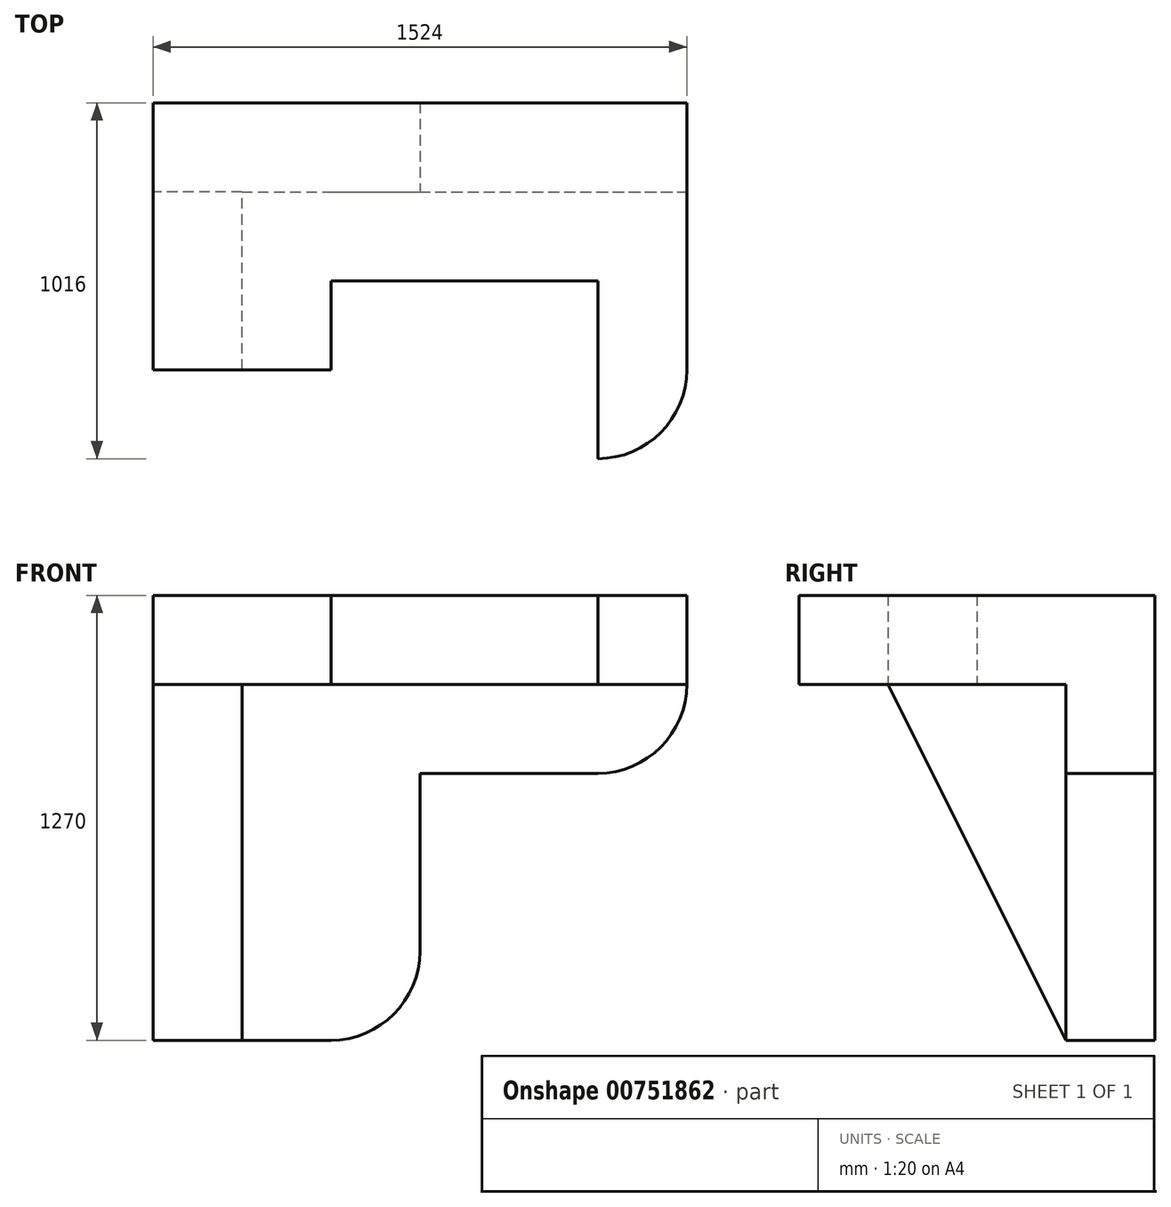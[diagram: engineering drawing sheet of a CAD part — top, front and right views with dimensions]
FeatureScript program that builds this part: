
annotation { "Feature Type Name" : "Feature", "Feature Type Description" : "" }
export const myFeature = defineFeature(function(context is Context, id is Id, definition is map)
    precondition{}
    {
        {
            var Q0;
            Q0=qCreatedBy(makeId("Front.planeOp"),FACE);
            var sketch = newSketch(context, id + "F0", { "sketchPlane" : qUnion([Q0])});
            skLineSegment(sketch, "E0", {"start": v(0, 508) * mm, "end": v(0, -762) * mm});
            skLineSegment(sketch, "E1", {"start": v(0, -762) * mm, "end": v(762, -762) * mm});
            skLineSegment(sketch, "E2", {"start": v(762, -762) * mm, "end": v(762, 0) * mm});
            skLineSegment(sketch, "E3", {"start": v(762, 0) * mm, "end": v(1524, 0) * mm});
            skLineSegment(sketch, "E4", {"start": v(1524, 0) * mm, "end": v(1524, 508) * mm});
            skLineSegment(sketch, "E5", {"start": v(1524, 508) * mm, "end": v(0, 508) * mm});
            skSolve(sketch);
        }
        {
            var Q0;
            Q0 = qSketchRegion(id + "F0", true);
            extrude(context, id + "F1", {"entities" : qUnion([Q0]), "depth" : 254 * mm, "offsetDistance" : 25.4 * mm});
        }
        {
            var Q0;
            Q0=makeQuery(id+"F1.opExtrude","CAP_FACE",FACE,{"disambiguationData":[OSD([sQuery(id+"F0.wireOp",EDGE,"E0"),sQuery(id+"F0.wireOp",EDGE,"E1"),sQuery(id+"F0.wireOp",EDGE,"E2"),sQuery(id+"F0.wireOp",EDGE,"E3"),sQuery(id+"F0.wireOp",EDGE,"E4"),sQuery(id+"F0.wireOp",EDGE,"E5")])],"isStart":false});
            var sketch = newSketch(context, id + "F2", { "sketchPlane" : qUnion([Q0])});
            skLineSegment(sketch, "E6.bottom", {"start": v(0, 254) * mm, "end": v(254, 254) * mm});
            skLineSegment(sketch, "E6.top", {"start": v(0, -762) * mm, "end": v(254, -762) * mm});
            skLineSegment(sketch, "E6.left", {"start": v(0, 254) * mm, "end": v(0, -762) * mm});
            skLineSegment(sketch, "E6.right", {"start": v(254, 254) * mm, "end": v(254, -762) * mm});
            skSolve(sketch);
        }
        {
            var Q0;
            Q0 = qSketchRegion(id + "F2", true);
            extrude(context, id + "F3", {"entities" : qUnion([Q0]), "operationType" : NewBodyOperationType.ADD, "depth" : 508 * mm, "offsetDistance" : 25.4 * mm});
        }
        {
            var Q0;
            Q0=makeQuery(id+"F3.boolean.opBoolean","MERGE",FACE,{"derivedFrom":[makeQuery(id+"F1.opExtrude","SWEPT_FACE",FACE,{"disambiguationData":[OSD([sQuery(id+"F0.wireOp",EDGE,"E0")])]}),makeQuery(id+"F3.opExtrude","SWEPT_FACE",FACE,{"disambiguationData":[OSD([sQuery(id+"F2.wireOp",EDGE,"E6.left")])]})]});
            var sketch = newSketch(context, id + "F4", { "sketchPlane" : qUnion([Q0])});
            skLineSegment(sketch, "E7", {"start": v(0, -762) * mm, "end": v(254, -762) * mm});
            skLineSegment(sketch, "E8", {"start": v(254, -762) * mm, "end": v(508, -762) * mm});
            skLineSegment(sketch, "E9", {"start": v(508, -762) * mm, "end": v(762, -762) * mm});
            skLineSegment(sketch, "E10", {"start": v(254, -762) * mm, "end": v(762, 254) * mm});
            skLineSegment(sketch, "E11", {"start": v(762, 254) * mm, "end": v(762, -762) * mm});
            skSolve(sketch);
        }
        {
            var Q0;
            Q0=makeQuery(id+"F4.imprint","IMPRINT",FACE,{"disambiguationData":[TD([[makeQuery(id+"F4.imprint","IMPRINT",EDGE,{"derivedFrom":sQuery(id+"F4.wireOp",EDGE,"E8")}),-1.0]])]});
            extrude(context, id + "F5", {"entities" : qUnion([Q0]), "operationType" : NewBodyOperationType.REMOVE, "oppositeDirection" : true, "depth" : 309.88 * mm, "offsetDistance" : 25.4 * mm});
        }
        {
            var Q0;
            Q0=makeQuery(id+"F1.opExtrude","CAP_FACE",FACE,{"disambiguationData":[OSD([sQuery(id+"F0.wireOp",EDGE,"E0"),sQuery(id+"F0.wireOp",EDGE,"E1"),sQuery(id+"F0.wireOp",EDGE,"E2"),sQuery(id+"F0.wireOp",EDGE,"E3"),sQuery(id+"F0.wireOp",EDGE,"E4"),sQuery(id+"F0.wireOp",EDGE,"E5")])],"isStart":false});
            var sketch = newSketch(context, id + "F6", { "sketchPlane" : qUnion([Q0])});
            skLineSegment(sketch, "E12.bottom", {"start": v(0, 508) * mm, "end": v(1524, 508) * mm});
            skLineSegment(sketch, "E12.top", {"start": v(0, 254) * mm, "end": v(1524, 254) * mm});
            skLineSegment(sketch, "E12.left", {"start": v(0, 508) * mm, "end": v(0, 254) * mm});
            skLineSegment(sketch, "E12.right", {"start": v(1524, 508) * mm, "end": v(1524, 254) * mm});
            skSolve(sketch);
        }
        {
            var Q0;
            Q0=makeQuery(id+"F6.imprint","IMPRINT",FACE,{"disambiguationData":[TD([[makeQuery(id+"F6.imprint","IMPRINT",EDGE,{"derivedFrom":sQuery(id+"F6.wireOp",EDGE,"E12.bottom")}),1.0]])]});
            extrude(context, id + "F7", {"entities" : qUnion([Q0]), "operationType" : NewBodyOperationType.ADD, "depth" : 508 * mm, "offsetDistance" : 25.4 * mm});
        }
        {
            var Q0;
            Q0=makeQuery(id+"F7.opExtrude","CAP_FACE",FACE,{"disambiguationData":[OSD([sQuery(id+"F6.wireOp",EDGE,"E12.bottom"),sQuery(id+"F6.wireOp",EDGE,"E12.top"),sQuery(id+"F6.wireOp",EDGE,"E12.left"),sQuery(id+"F6.wireOp",EDGE,"E12.right")])],"isStart":false});
            var sketch = newSketch(context, id + "F8", { "sketchPlane" : qUnion([Q0])});
            skLineSegment(sketch, "E13", {"start": v(0, 508) * mm, "end": v(254, 508) * mm});
            skLineSegment(sketch, "E14", {"start": v(254, 508) * mm, "end": v(508, 508) * mm});
            skLineSegment(sketch, "E15", {"start": v(508, 508) * mm, "end": v(762, 508) * mm});
            skLineSegment(sketch, "E16", {"start": v(762, 508) * mm, "end": v(1016, 508) * mm});
            skLineSegment(sketch, "E17", {"start": v(1016, 508) * mm, "end": v(1270, 508) * mm});
            skLineSegment(sketch, "E18", {"start": v(1270, 508) * mm, "end": v(1524, 508) * mm});
            skLineSegment(sketch, "E19", {"start": v(508, 508) * mm, "end": v(508, 254) * mm});
            skLineSegment(sketch, "E20", {"start": v(508, 254) * mm, "end": v(1270, 254) * mm});
            skLineSegment(sketch, "E21", {"start": v(1270, 254) * mm, "end": v(1270, 508) * mm});
            skSolve(sketch);
        }
        {
            var Q0;
            Q0=makeQuery(id+"F8.imprint","IMPRINT",FACE,{"disambiguationData":[TD([[makeQuery(id+"F8.imprint","IMPRINT",EDGE,{"derivedFrom":sQuery(id+"F8.wireOp",EDGE,"E15")}),1.0]])]});
            extrude(context, id + "F9", {"entities" : qUnion([Q0]), "operationType" : NewBodyOperationType.REMOVE, "oppositeDirection" : true, "depth" : 254 * mm, "offsetDistance" : 25.4 * mm});
        }
        {
            var Q0;
            {var subQ0=sQuery(id+"F6.wireOp",EDGE,"E12.top");var subQ1=sQuery(id+"F6.wireOp",EDGE,"E12.bottom");var subQ2=sQuery(id+"F6.wireOp",EDGE,"E12.right");Q0=makeQuery(id+"F9.boolean.opBoolean","SPLIT",FACE,{"disambiguationData":[TD([makeQuery(id+"F1.opExtrude","SWEPT_FACE",FACE,{"disambiguationData":[OSD([sQuery(id+"F0.wireOp",EDGE,"E4")])]})])],"derivedFrom":makeQuery(id+"F7.opExtrude","CAP_FACE",FACE,{"disambiguationData":[OSD([subQ1,subQ0,sQuery(id+"F6.wireOp",EDGE,"E12.left"),subQ2])],"isStart":false})});}
            var sketch = newSketch(context, id + "F10", { "sketchPlane" : qUnion([Q0])});
            skLineSegment(sketch, "E22.bottom", {"start": v(1270, 508) * mm, "end": v(1524, 508) * mm});
            skLineSegment(sketch, "E22.top", {"start": v(1270, 254) * mm, "end": v(1524, 254) * mm});
            skLineSegment(sketch, "E22.left", {"start": v(1270, 508) * mm, "end": v(1270, 254) * mm});
            skLineSegment(sketch, "E22.right", {"start": v(1524, 508) * mm, "end": v(1524, 254) * mm});
            skSolve(sketch);
        }
        {
            var Q0;
            Q0=makeQuery(id+"F10.imprint","IMPRINT",FACE,{"disambiguationData":[TD([[makeQuery(id+"F10.imprint","IMPRINT",EDGE,{"derivedFrom":sQuery(id+"F10.wireOp",EDGE,"E22.bottom")}),1.0]])]});
            extrude(context, id + "F11", {"entities" : qUnion([Q0]), "operationType" : NewBodyOperationType.ADD, "depth" : 254 * mm, "offsetDistance" : 25.4 * mm});
        }
        {
            var Q0;
            Q0=makeQuery(id+"F1.opExtrude","CAP_FACE",FACE,{"disambiguationData":[OSD([sQuery(id+"F0.wireOp",EDGE,"E0"),sQuery(id+"F0.wireOp",EDGE,"E1"),sQuery(id+"F0.wireOp",EDGE,"E2"),sQuery(id+"F0.wireOp",EDGE,"E3"),sQuery(id+"F0.wireOp",EDGE,"E4"),sQuery(id+"F0.wireOp",EDGE,"E5")])],"isStart":false});
            var sketch = newSketch(context, id + "F12", { "sketchPlane" : qUnion([Q0])});
            skLineSegment(sketch, "E23", {"start": v(254, -762) * mm, "end": v(508, -762) * mm});
            skLineSegment(sketch, "E24", {"start": v(762, -508) * mm, "end": v(762, -254) * mm});
            skLineSegment(sketch, "E25", {"start": v(762, -254) * mm, "end": v(762, 0) * mm});
            skArc(sketch, "E26", {"start": v(508, -762) * mm, "mid": v(687.6, -687.6) * mm, "end": v(762, -508) * mm});
            skSolve(sketch);
        }
        {
            var Q0;
            {var subQ0=sQuery(id+"F12.wireOp",EDGE,"E26");Q0=makeQuery(id+"F12.imprint","IMPRINT",FACE,{"disambiguationData":[TD([[makeQuery(id+"F12.imprint","IMPRINT",EDGE,{"derivedFrom":subQ0}),-1.0]])]});}
            extrude(context, id + "F13", {"entities" : qUnion([Q0]), "operationType" : NewBodyOperationType.REMOVE, "oppositeDirection" : true, "depth" : 254 * mm, "offsetDistance" : 25.4 * mm});
        }
        {
            var Q0;
            Q0=makeQuery(id+"F1.opExtrude","CAP_FACE",FACE,{"disambiguationData":[OSD([sQuery(id+"F0.wireOp",EDGE,"E0"),sQuery(id+"F0.wireOp",EDGE,"E1"),sQuery(id+"F0.wireOp",EDGE,"E2"),sQuery(id+"F0.wireOp",EDGE,"E3"),sQuery(id+"F0.wireOp",EDGE,"E4"),sQuery(id+"F0.wireOp",EDGE,"E5")])],"isStart":false});
            var sketch = newSketch(context, id + "F14", { "sketchPlane" : qUnion([Q0])});
            skLineSegment(sketch, "E27", {"start": v(1524, 254) * mm, "end": v(1524, 0) * mm});
            skLineSegment(sketch, "E28", {"start": v(1524, 0) * mm, "end": v(1270, 0) * mm});
            skArc(sketch, "E29", {"start": v(1270, 0) * mm, "mid": v(1449.6, 74.4) * mm, "end": v(1524, 254) * mm});
            skSolve(sketch);
        }
        {
            var Q0;
            Q0=makeQuery(id+"F14.imprint","IMPRINT",FACE,{"disambiguationData":[TD([[makeQuery(id+"F14.imprint","IMPRINT",EDGE,{"derivedFrom":sQuery(id+"F14.wireOp",EDGE,"E27")}),1.0]])]});
            extrude(context, id + "F15", {"entities" : qUnion([Q0]), "operationType" : NewBodyOperationType.REMOVE, "oppositeDirection" : true, "depth" : 254 * mm, "offsetDistance" : 25.4 * mm});
        }
        {
            var Q0;
            Q0=makeQuery(id+"F11.boolean.opBoolean","MERGE",FACE,{"derivedFrom":[makeQuery(id+"F7.opExtrude","SWEPT_FACE",FACE,{"disambiguationData":[OSD([sQuery(id+"F6.wireOp",EDGE,"E12.top")])]}),makeQuery(id+"F11.opExtrude","SWEPT_FACE",FACE,{"disambiguationData":[OSD([sQuery(id+"F10.wireOp",EDGE,"E22.top")])]})]});
            var sketch = newSketch(context, id + "F16", { "sketchPlane" : qUnion([Q0])});
            skLineSegment(sketch, "E30", {"start": v(1270, 1016) * mm, "end": v(1270, 762) * mm});
            skLineSegment(sketch, "E31", {"start": v(1270, 762) * mm, "end": v(1270, 508) * mm});
            skLineSegment(sketch, "E32", {"start": v(1524, 1016) * mm, "end": v(1524, 762) * mm});
            skLineSegment(sketch, "E33", {"start": v(1524, 762) * mm, "end": v(1524, 508) * mm});
            skArc(sketch, "E34", {"start": v(1524, 762) * mm, "mid": v(1449.6, 941.6) * mm, "end": v(1270, 1016) * mm});
            skSolve(sketch);
        }
        {
            var Q0;
            Q0=makeQuery(id+"F16.imprint","IMPRINT",FACE,{"disambiguationData":[TD([[makeQuery(id+"F16.imprint","IMPRINT",EDGE,{"derivedFrom":sQuery(id+"F16.wireOp",EDGE,"E32")}),-1.0]])]});
            extrude(context, id + "F17", {"entities" : qUnion([Q0]), "operationType" : NewBodyOperationType.REMOVE, "oppositeDirection" : true, "depth" : 254 * mm, "offsetDistance" : 25.4 * mm});
        }
    });
